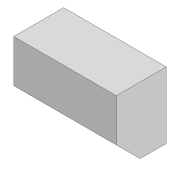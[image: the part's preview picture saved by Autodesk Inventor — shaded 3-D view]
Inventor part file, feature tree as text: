
AUTODESK INVENTOR PART (.ipt)
format: ipt  version: 2020 (Build 240168000, 168)  size: 144,384 bytes
history: native  units: in
note: dims shown in document units (in); Inventor stores cm internally (conversion verified against a paired STEP export)
features: extrude x5, sketch x5, projected_geometry x3
ambient origin geometry x8: Origin, YZ Plane, XZ Plane, XY Plane, X Axis, Y Axis, Z Axis, Center Point
bodies: Solid1 (feature_tree)
feature tree (13):
  extrude  "Extrusion1"  Depth=4.5276in
  extrude  "Extrusion2"  Depth=8.6614in
  extrude  "Extrusion3"  TaperAngle=0.0deg  [1 undecoded]
  extrude  "Extrusion4"  Depth=5.5in
  extrude  "Extrusion5"  Depth=0.1969in TaperAngle=0.0deg
  sketch  "Sketch1"  dims[d0=6.9882in d1=4.5276in]
  sketch  "Sketch2"  dims[d2=8.6614in d3=8.6614in]
  projected_geometry  "Projected Loop1"
  sketch  "Sketch3"  dims[d4=0.0in d5=0.0in]
  sketch  "Sketch4"  dims[d6=8.5in d7=5.5in]
  projected_geometry  "Projected Loop2"
  sketch  "Sketch5"  dims[d8=0.1969in d9=0.1969in d10=0.0in d11=0.1969in d12=1.9685in d13=0.0in d14=1.9685in d15=45.0deg d16=0.1969in d17=0.0in d18=0.1969in d19=0.1969in d20=0.0in d21=0.1969in d22=0.0in]
  projected_geometry  "Projected Loop3"
note: 1 required parameter value undecoded (feature->parameter linkage not recoverable at this tier; creation-order binding heuristic only, values carry confidence <= 0.55)
